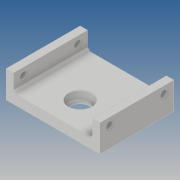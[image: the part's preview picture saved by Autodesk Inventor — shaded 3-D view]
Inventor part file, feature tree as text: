
AUTODESK INVENTOR PART (.ipt)
format: ipt  version: 2019 (Build 230136000, 136)  size: 122,368 bytes
history: native  units: mm
features: other x3, sketch x2, extrude x1, hole x1, projected_geometry x1
ambient origin geometry x8: Origin, YZ Plane, XZ Plane, XY Plane, X Axis, Y Axis, Z Axis, Center Point
bodies: Solide1 (feature_tree)
feature tree (8):
  other  "base_cloison.ipt"
  extrude  "Extrusion1"  Depth=10.0mm
  hole  "Perçage1"  [1 undecoded]
  other  "Solide1::base_cloison.ipt"
  other  "FonctionRepérage1"
  sketch  "Esquisse2"
  sketch  "Esquisse3"
  projected_geometry  "Boucle projetée1"
note: 1 required parameter value undecoded (feature->parameter linkage not recoverable at this tier; creation-order binding heuristic only, values carry confidence <= 0.55)
